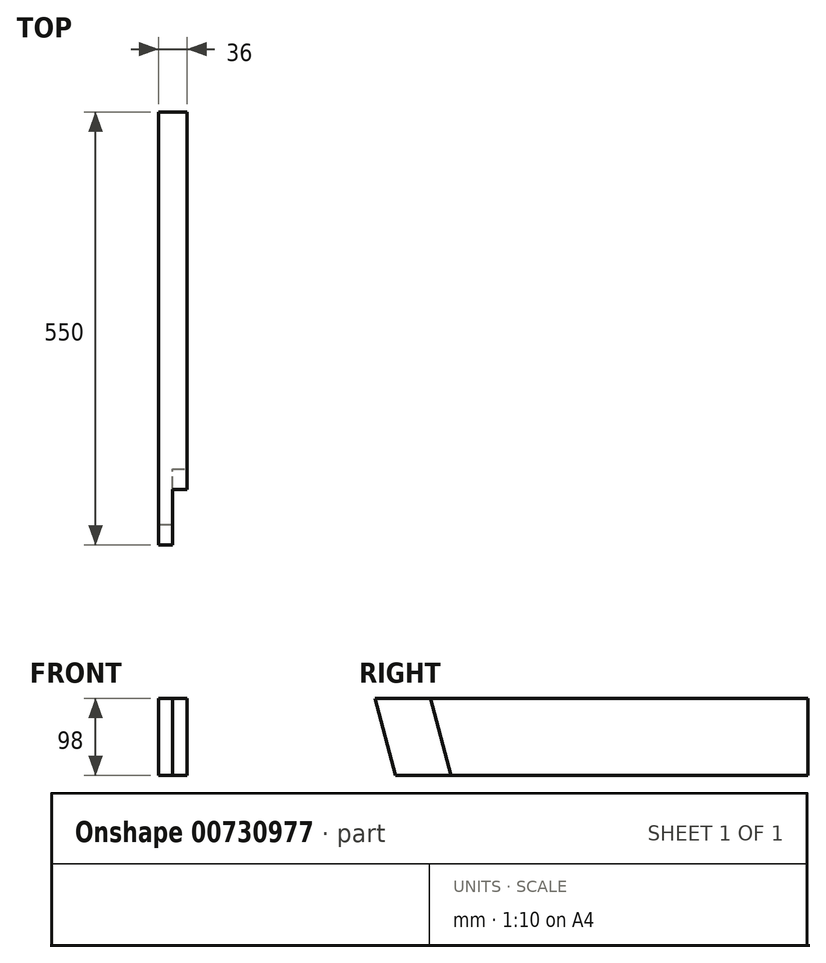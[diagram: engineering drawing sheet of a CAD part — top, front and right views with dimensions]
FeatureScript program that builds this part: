
annotation { "Feature Type Name" : "Feature", "Feature Type Description" : "" }
export const myFeature = defineFeature(function(context is Context, id is Id, definition is map)
    precondition{}
    {
        {
            var Q0;
            Q0=qCreatedBy(makeId("Front.planeOp"),FACE);
            var sketch = newSketch(context, id + "F0", { "sketchPlane" : qUnion([Q0])});
            skLineSegment(sketch, "E0.bottom", {"start": v(18, -49) * mm, "end": v(-18, -49) * mm});
            skLineSegment(sketch, "E0.top", {"start": v(18, 49) * mm, "end": v(-18, 49) * mm});
            skLineSegment(sketch, "E0.left", {"start": v(18, -49) * mm, "end": v(18, 49) * mm});
            skLineSegment(sketch, "E0.right", {"start": v(-18, -49) * mm, "end": v(-18, 49) * mm});
            skPoint(sketch, "E0.middle", {"position": v(0, 0) * mm});
            skSolve(sketch);
        }
        {
            var Q0;
            Q0=makeQuery(id+"F0.imprint","IMPRINT",FACE,{"disambiguationData":[TD([[makeQuery(id+"F0.imprint","IMPRINT",EDGE,{"derivedFrom":sQuery(id+"F0.wireOp",EDGE,"E0.bottom")}),-1.0]])]});
            extrude(context, id + "F1", {"entities" : qUnion([Q0]), "depth" : 550 * mm, "offsetDistance" : 25 * mm});
        }
        {
            var Q0;
            Q0=makeQuery(id+"F1.opExtrude","SWEPT_FACE",FACE,{"disambiguationData":[OSD([sQuery(id+"F0.wireOp",EDGE,"E0.left")])]});
            var sketch = newSketch(context, id + "F2", { "sketchPlane" : qUnion([Q0])});
            skLineSegment(sketch, "E1", {"start": v(-550, 49) * mm, "end": v(-523.74, -49) * mm});
            skLineSegment(sketch, "E2", {"start": v(-523.74, -49) * mm, "end": v(-550, -49) * mm});
            skLineSegment(sketch, "E3", {"start": v(-550, -49) * mm, "end": v(-550, 49) * mm});
            skSolve(sketch);
        }
        {
            var Q0;
            Q0=makeQuery(id+"F2.imprint","IMPRINT",FACE,{"disambiguationData":[TD([[makeQuery(id+"F2.imprint","IMPRINT",EDGE,{"derivedFrom":sQuery(id+"F2.wireOp",EDGE,"E1")}),-1.0]])]});
            extrude(context, id + "F3", {"entities" : qUnion([Q0]), "operationType" : NewBodyOperationType.REMOVE, "endBound" : BoundingType.UP_TO_NEXT, "oppositeDirection" : true, "depth" : 25 * mm, "offsetDistance" : 25 * mm});
        }
        {
            var Q0;
            Q0=makeQuery(id+"F1.opExtrude","SWEPT_FACE",FACE,{"disambiguationData":[OSD([sQuery(id+"F0.wireOp",EDGE,"E0.left")])]});
            var sketch = newSketch(context, id + "F4", { "sketchPlane" : qUnion([Q0])});
            skLineSegment(sketch, "E4", {"start": v(-550, 49) * mm, "end": v(-479.5, 49) * mm});
            skLineSegment(sketch, "E5", {"start": v(-479.5, 49) * mm, "end": v(-453.24, -49) * mm});
            skLineSegment(sketch, "E6", {"start": v(-453.24, -49) * mm, "end": v(-523.74, -49) * mm});
            skLineSegment(sketch, "E7", {"start": v(-523.74, -49) * mm, "end": v(-550, 49) * mm});
            skSolve(sketch);
        }
        {
            var Q0;
            Q0=makeQuery(id+"F4.imprint","IMPRINT",FACE,{"disambiguationData":[TD([[makeQuery(id+"F4.imprint","IMPRINT",EDGE,{"derivedFrom":sQuery(id+"F4.wireOp",EDGE,"E4")}),-1.0]])]});
            extrude(context, id + "F5", {"entities" : qUnion([Q0]), "operationType" : NewBodyOperationType.REMOVE, "depth" : -18 * mm, "offsetDistance" : 25 * mm});
        }
    });
